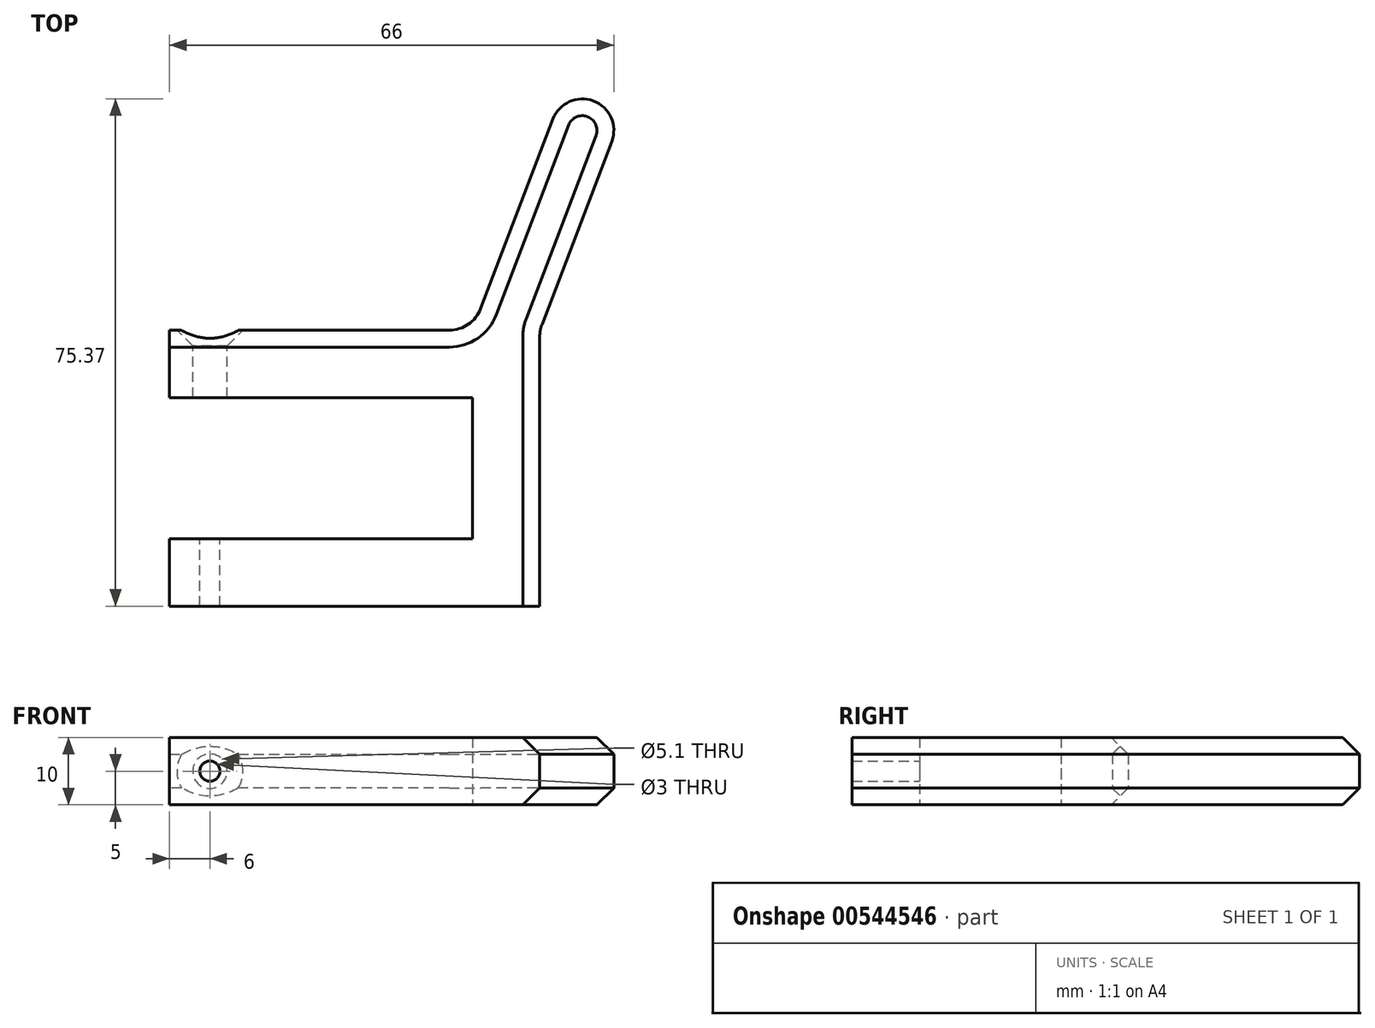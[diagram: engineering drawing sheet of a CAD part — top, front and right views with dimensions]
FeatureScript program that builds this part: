
annotation { "Feature Type Name" : "Feature", "Feature Type Description" : "" }
export const myFeature = defineFeature(function(context is Context, id is Id, definition is map)
    precondition{}
    {
        {
            var Q0;
            Q0=qCreatedBy(makeId("Top.planeOp"),FACE);
            var sketch = newSketch(context, id + "F0", { "sketchPlane" : qUnion([Q0])});
            skLineSegment(sketch, "E0.bottom", {"start": v(0, 20.5) * mm, "end": v(41.56, 20.5) * mm});
            skLineSegment(sketch, "E0.top", {"start": v(0, 10.5) * mm, "end": v(45, 10.5) * mm});
            skLineSegment(sketch, "E0.left", {"start": v(0, 20.5) * mm, "end": v(0, 10.5) * mm});
            skLineSegment(sketch, "E1.bottom", {"start": v(0, -10.5) * mm, "end": v(45, -10.5) * mm});
            skLineSegment(sketch, "E1.top", {"start": v(0, -20.5) * mm, "end": v(45, -20.5) * mm});
            skLineSegment(sketch, "E1.left", {"start": v(0, -10.5) * mm, "end": v(0, -20.5) * mm});
            skLineSegment(sketch, "E2.bottom", {"start": v(45, 20.5) * mm, "end": v(55, 20.5) * mm});
            skLineSegment(sketch, "E2.top", {"start": v(45, -20.5) * mm, "end": v(55, -20.5) * mm});
            skLineSegment(sketch, "E2.left", {"start": v(45, 10.5) * mm, "end": v(45, -10.5) * mm});
            skLineSegment(sketch, "E2.right", {"start": v(55, 19.58) * mm, "end": v(55, -20.5) * mm});
            skLineSegment(sketch, "E3", {"start": v(46.23, 23.72) * mm, "end": v(56.96, 51.86) * mm});
            skLineSegment(sketch, "E4", {"start": v(55.33, 21.36) * mm, "end": v(65.69, 48.53) * mm});
            skLineSegment(sketch, "E5", {"start": v(65.69, 48.53) * mm, "end": v(56.96, 51.86) * mm, "construction": true});
            skArc(sketch, "E6", {"start": v(65.69, 48.53) * mm, "mid": v(62.99, 54.56) * mm, "end": v(56.96, 51.86) * mm});
            skPoint(sketch, "E7.visualSharp", {"position": v(45, 20.5) * mm});
            skArc(sketch, "E7.filletArc", {"start": v(41.56, 20.5) * mm, "mid": v(44.4, 21.38) * mm, "end": v(46.23, 23.72) * mm});
            skPoint(sketch, "E8.visualSharp", {"position": v(55, 20.5) * mm});
            skArc(sketch, "E8.filletArc", {"start": v(55.33, 21.36) * mm, "mid": v(55.08, 20.48) * mm, "end": v(55, 19.58) * mm});
            skSolve(sketch);
        }
        {
            var Q0;
            Q0 = qSketchRegion(id + "F0", true);
            extrude(context, id + "F1", {"entities" : qUnion([Q0]), "depth" : 10 * mm, "offsetDistance" : 25 * mm});
        }
        {
            var Q0;
            Q0=makeQuery(id+"F1.opExtrude","SWEPT_FACE",FACE,{"disambiguationData":[OSD([sQuery(id+"F0.wireOp",EDGE,"E0.bottom")])]});
            var sketch = newSketch(context, id + "F2", { "sketchPlane" : qUnion([Q0])});
            skPoint(sketch, "E9", {"position": v(-6, 5) * mm});
            skPoint(sketch, "E9.positionSnap0", {"position": v(0, 5) * mm});
            skSolve(sketch);
        }
        {
            var Q0;
            Q0=sQuery(id+"F2.wireOp",VERTEX,"E9");
            var Q1;
            Q1=makeQuery(id+"F1.opExtrude","SWEPT_BODY",BODY,{"disambiguationData":[OSD([sQuery(id+"F0.wireOp",EDGE,"E0.bottom"),sQuery(id+"F0.wireOp",EDGE,"E0.top"),sQuery(id+"F0.wireOp",EDGE,"E0.left"),sQuery(id+"F0.wireOp",EDGE,"E1.bottom"),sQuery(id+"F0.wireOp",EDGE,"E1.top"),sQuery(id+"F0.wireOp",EDGE,"E1.left"),sQuery(id+"F0.wireOp",EDGE,"E2.top"),sQuery(id+"F0.wireOp",EDGE,"E2.left"),sQuery(id+"F0.wireOp",EDGE,"E2.right"),sQuery(id+"F0.wireOp",EDGE,"E3"),sQuery(id+"F0.wireOp",EDGE,"E4"),sQuery(id+"F0.wireOp",EDGE,"E6"),sQuery(id+"F0.wireOp",EDGE,"E7.filletArc"),sQuery(id+"F0.wireOp",EDGE,"E8.filletArc")])]});
            hole(context, id + "F3", {"style" : HoleStyle.C_SINK, "endStyle" : HoleEndStyle.BLIND, "holeDiameter" : 5.1 * mm, "cSinkDiameter" : 9.8 * mm, "cSinkAngle" : 90 * degree, "holeDepth" : 20 * mm, "isTappedThrough" : true, "tappedDepth" : 12 * mm, "tapClearance" : 3, "locations" : qUnion([Q0]), "scope" : qUnion([Q1])});
        }
        {
            var Q0;
            Q0=makeQuery(id+"F1.opExtrude","SWEPT_FACE",FACE,{"disambiguationData":[OSD([sQuery(id+"F0.wireOp",EDGE,"E1.bottom")])]});
            var sketch = newSketch(context, id + "F4", { "sketchPlane" : qUnion([Q0])});
            skPoint(sketch, "E10.0", {"position": v(-6, 5) * mm});
            skSolve(sketch);
        }
        {
            var Q0;
            Q0=sQuery(id+"F4.wireOp",VERTEX,"E10.0");
            var Q1;
            Q1=makeQuery(id+"F1.opExtrude","SWEPT_BODY",BODY,{"disambiguationData":[OSD([sQuery(id+"F0.wireOp",EDGE,"E0.bottom"),sQuery(id+"F0.wireOp",EDGE,"E0.top"),sQuery(id+"F0.wireOp",EDGE,"E0.left"),sQuery(id+"F0.wireOp",EDGE,"E1.bottom"),sQuery(id+"F0.wireOp",EDGE,"E1.top"),sQuery(id+"F0.wireOp",EDGE,"E1.left"),sQuery(id+"F0.wireOp",EDGE,"E2.top"),sQuery(id+"F0.wireOp",EDGE,"E2.left"),sQuery(id+"F0.wireOp",EDGE,"E2.right"),sQuery(id+"F0.wireOp",EDGE,"E3"),sQuery(id+"F0.wireOp",EDGE,"E4"),sQuery(id+"F0.wireOp",EDGE,"E6"),sQuery(id+"F0.wireOp",EDGE,"E7.filletArc"),sQuery(id+"F0.wireOp",EDGE,"E8.filletArc")])]});
            hole(context, id + "F5", {"style" : HoleStyle.SIMPLE, "endStyle" : HoleEndStyle.THROUGH, "holeDiameter" : 3 * mm, "isTappedThrough" : true, "tappedDepth" : 12 * mm, "tapClearance" : 3, "locations" : qUnion([Q0]), "scope" : qUnion([Q1])});
        }
        {
            var Q0;
            Q0=makeQuery(id+"F1.opExtrude","SWEPT_FACE",FACE,{"disambiguationData":[OSD([sQuery(id+"F0.wireOp",EDGE,"E6")])]});
            chamfer(context, id + "F6", {"entities" : qUnion([Q0]), "width" : 2.5 * mm, "tangentPropagation" : true});
        }
    });
